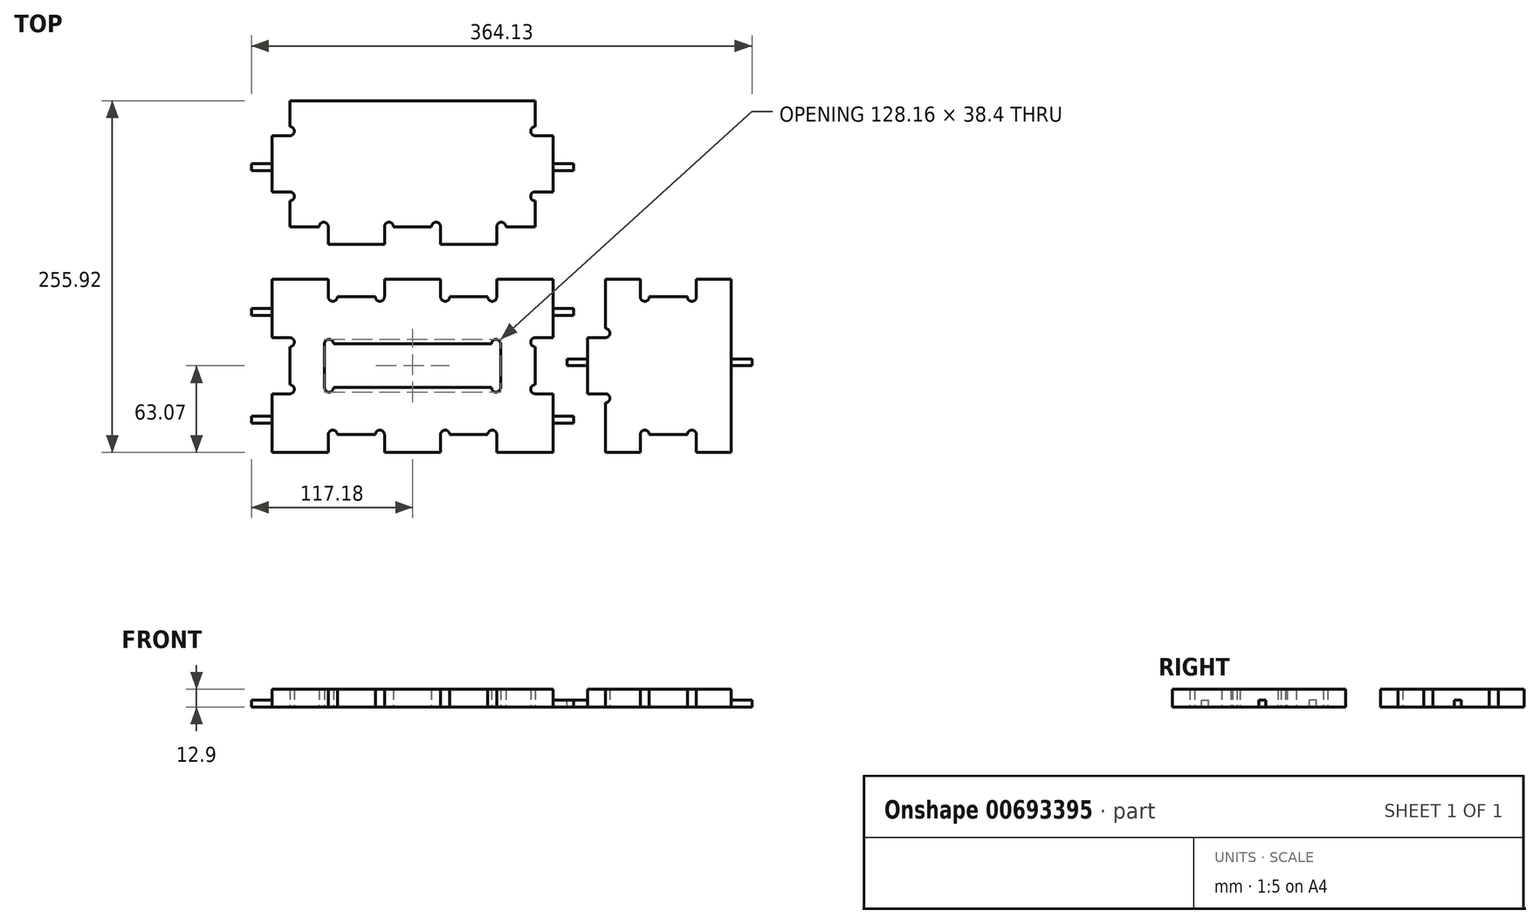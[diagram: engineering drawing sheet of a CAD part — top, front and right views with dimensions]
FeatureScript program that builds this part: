
annotation { "Feature Type Name" : "Feature", "Feature Type Description" : "" }
export const myFeature = defineFeature(function(context is Context, id is Id, definition is map)
    precondition{}
    {
        {
            assignVariable(context, id + "F0", {"name" : "thick", "anyValue" : 12.9 * mm});
        }
        {
            var Q0;
            Q0=qCreatedBy(makeId("Top.planeOp"),FACE);
            var sketch = newSketch(context, id + "F1", { "sketchPlane" : qUnion([Q0])});
            skLineSegment(sketch, "E0.bottom", {"start": v(64.08, -15.9) * mm, "end": v(-64.08, -15.9) * mm});
            skLineSegment(sketch, "E0.top", {"start": v(64.08, 15.9) * mm, "end": v(-64.08, 15.9) * mm});
            skLineSegment(sketch, "E0.left", {"start": v(64.08, -15.9) * mm, "end": v(64.08, 15.9) * mm});
            skLineSegment(sketch, "E0.right", {"start": v(-64.08, -15.9) * mm, "end": v(-64.08, 15.9) * mm});
            skPoint(sketch, "E0.middle", {"position": v(0, 0) * mm});
            skLineSegment(sketch, "E1", {"start": v(-102.18, 63.07) * mm, "end": v(-61.3, 63.07) * mm});
            skLineSegment(sketch, "E2", {"start": v(102.18, 63.07) * mm, "end": v(102.18, -63.07) * mm});
            skLineSegment(sketch, "E3", {"start": v(102.18, -63.07) * mm, "end": v(-102.18, -63.07) * mm});
            skLineSegment(sketch, "E4", {"start": v(-102.18, -63.07) * mm, "end": v(-102.18, 63.07) * mm});
            skPoint(sketch, "E5", {"position": v(0, 63.07) * mm});
            skPoint(sketch, "E6", {"position": v(102.18, 0) * mm});
            skLineSegment(sketch, "E7", {"start": v(-102.18, -63.07) * mm, "end": v(102.18, 63.07) * mm, "construction": true});
            skCircle(sketch, "E8", {"center": v(-60.78, 15.9) * mm, "radius": 3.3 * mm});
            skCircle(sketch, "E9", {"center": v(-60.78, -15.9) * mm, "radius": 3.3 * mm});
            skCircle(sketch, "E10", {"center": v(60.78, -15.9) * mm, "radius": 3.3 * mm});
            skCircle(sketch, "E11", {"center": v(60.78, 15.9) * mm, "radius": 3.3 * mm});
            skLineSegment(sketch, "E12", {"start": v(-61.3, 50.17) * mm, "end": v(-20.44, 50.17) * mm});
            skLineSegment(sketch, "E13", {"start": v(20.44, 50.17) * mm, "end": v(61.3, 50.17) * mm});
            skLineSegment(sketch, "E14", {"start": v(-61.3, 50.17) * mm, "end": v(-61.3, 63.07) * mm});
            skLineSegment(sketch, "E15", {"start": v(-20.44, 50.17) * mm, "end": v(-20.44, 63.07) * mm});
            skLineSegment(sketch, "E16", {"start": v(20.44, 50.17) * mm, "end": v(20.44, 63.07) * mm});
            skLineSegment(sketch, "E17", {"start": v(61.3, 50.17) * mm, "end": v(61.3, 63.07) * mm});
            skLineSegment(sketch, "E18", {"start": v(-61.3, 63.07) * mm, "end": v(-20.44, 63.07) * mm});
            skLineSegment(sketch, "E19", {"start": v(-20.44, 63.07) * mm, "end": v(20.44, 63.07) * mm});
            skLineSegment(sketch, "E20", {"start": v(20.44, 63.07) * mm, "end": v(61.3, 63.07) * mm});
            skLineSegment(sketch, "E21", {"start": v(61.3, 63.07) * mm, "end": v(102.18, 63.07) * mm});
            skLineSegment(sketch, "E22", {"start": v(-61.3, -63.07) * mm, "end": v(-61.3, -50.17) * mm});
            skLineSegment(sketch, "E23", {"start": v(-61.3, -50.17) * mm, "end": v(-20.44, -50.17) * mm});
            skLineSegment(sketch, "E24", {"start": v(-20.44, -50.17) * mm, "end": v(-20.44, -63.07) * mm});
            skLineSegment(sketch, "E25", {"start": v(20.44, -63.07) * mm, "end": v(20.44, -50.17) * mm});
            skLineSegment(sketch, "E26", {"start": v(20.44, -50.17) * mm, "end": v(61.3, -50.17) * mm});
            skLineSegment(sketch, "E27", {"start": v(61.3, -50.17) * mm, "end": v(61.3, -63.07) * mm});
            skLineSegment(sketch, "E28", {"start": v(102.18, 20.44) * mm, "end": v(89.28, 20.44) * mm});
            skLineSegment(sketch, "E29", {"start": v(89.28, 20.44) * mm, "end": v(89.28, -20.44) * mm});
            skLineSegment(sketch, "E30", {"start": v(89.28, -20.44) * mm, "end": v(102.18, -20.44) * mm});
            skPoint(sketch, "E31", {"position": v(89.28, 0) * mm});
            skLineSegment(sketch, "E32", {"start": v(-102.18, 20.44) * mm, "end": v(-89.28, 20.44) * mm});
            skLineSegment(sketch, "E33", {"start": v(-89.28, 20.44) * mm, "end": v(-89.28, -20.44) * mm});
            skLineSegment(sketch, "E34", {"start": v(-89.28, -20.44) * mm, "end": v(-102.18, -20.44) * mm});
            skCircle(sketch, "E35", {"center": v(-58, 50.17) * mm, "radius": 3.3 * mm});
            skCircle(sketch, "E36", {"center": v(-23.74, 50.17) * mm, "radius": 3.3 * mm});
            skCircle(sketch, "E37", {"center": v(23.74, 50.17) * mm, "radius": 3.3 * mm});
            skCircle(sketch, "E38", {"center": v(58, 50.17) * mm, "radius": 3.3 * mm});
            skCircle(sketch, "E39", {"center": v(89.28, 17.13) * mm, "radius": 3.3 * mm});
            skCircle(sketch, "E40", {"center": v(89.28, -17.13) * mm, "radius": 3.3 * mm});
            skCircle(sketch, "E41", {"center": v(58, -50.17) * mm, "radius": 3.3 * mm});
            skCircle(sketch, "E42", {"center": v(23.74, -50.17) * mm, "radius": 3.3 * mm});
            skCircle(sketch, "E43", {"center": v(-23.74, -50.17) * mm, "radius": 3.3 * mm});
            skCircle(sketch, "E44", {"center": v(-58, -50.17) * mm, "radius": 3.3 * mm});
            skCircle(sketch, "E45", {"center": v(-89.28, -17.13) * mm, "radius": 3.3 * mm});
            skCircle(sketch, "E46", {"center": v(-89.28, 17.13) * mm, "radius": 3.3 * mm});
            skLineSegment(sketch, "E47", {"start": v(-89.28, 101.17) * mm, "end": v(89.28, 101.17) * mm});
            skLineSegment(sketch, "E48", {"start": v(89.28, 101.17) * mm, "end": v(89.28, 192.85) * mm});
            skLineSegment(sketch, "E49", {"start": v(89.28, 192.85) * mm, "end": v(-89.28, 192.85) * mm});
            skLineSegment(sketch, "E50", {"start": v(-89.28, 192.85) * mm, "end": v(-89.28, 101.17) * mm});
            skLineSegment(sketch, "E51", {"start": v(-61.3, 101.17) * mm, "end": v(-61.3, 88.27) * mm});
            skLineSegment(sketch, "E52", {"start": v(-61.3, 88.27) * mm, "end": v(-20.44, 88.27) * mm});
            skLineSegment(sketch, "E53", {"start": v(-20.44, 88.27) * mm, "end": v(-20.44, 101.17) * mm});
            skLineSegment(sketch, "E54", {"start": v(20.44, 101.17) * mm, "end": v(20.44, 88.27) * mm});
            skLineSegment(sketch, "E55", {"start": v(20.44, 88.27) * mm, "end": v(61.3, 88.27) * mm});
            skLineSegment(sketch, "E56", {"start": v(61.3, 88.27) * mm, "end": v(61.3, 101.17) * mm});
            skCircle(sketch, "E57", {"center": v(17.13, 101.17) * mm, "radius": 3.3 * mm});
            skCircle(sketch, "E58", {"center": v(-17.13, 101.17) * mm, "radius": 3.3 * mm});
            skCircle(sketch, "E59", {"center": v(-64.61, 101.17) * mm, "radius": 3.3 * mm});
            skCircle(sketch, "E60", {"center": v(64.61, 101.17) * mm, "radius": 3.3 * mm});
            skLineSegment(sketch, "E61", {"start": v(102.18, 167.45) * mm, "end": v(102.18, 126.57) * mm});
            skPoint(sketch, "E62", {"position": v(89.28, 147.01) * mm});
            skPoint(sketch, "E63", {"position": v(102.18, 147.01) * mm});
            skLineSegment(sketch, "E64", {"start": v(102.18, 167.45) * mm, "end": v(89.28, 167.45) * mm});
            skLineSegment(sketch, "E65", {"start": v(102.18, 126.57) * mm, "end": v(89.28, 126.57) * mm});
            skCircle(sketch, "E66", {"center": v(89.28, 123.27) * mm, "radius": 3.3 * mm});
            skCircle(sketch, "E67", {"center": v(89.28, 170.75) * mm, "radius": 3.3 * mm});
            skLineSegment(sketch, "E68", {"start": v(-89.28, 126.57) * mm, "end": v(-102.18, 126.57) * mm});
            skLineSegment(sketch, "E69", {"start": v(-102.18, 126.57) * mm, "end": v(-102.18, 167.45) * mm});
            skLineSegment(sketch, "E70", {"start": v(-102.18, 167.45) * mm, "end": v(-89.28, 167.45) * mm});
            skCircle(sketch, "E71", {"center": v(-89.28, 170.75) * mm, "radius": 3.3 * mm});
            skCircle(sketch, "E72", {"center": v(-89.28, 123.27) * mm, "radius": 3.3 * mm});
            skLineSegment(sketch, "E73", {"start": v(140.28, 63.07) * mm, "end": v(140.28, -63.07) * mm});
            skLineSegment(sketch, "E74", {"start": v(231.95, -63.07) * mm, "end": v(231.95, 63.07) * mm});
            skLineSegment(sketch, "E75", {"start": v(231.95, 63.07) * mm, "end": v(140.28, 63.07) * mm});
            skLineSegment(sketch, "E76", {"start": v(140.28, 20.44) * mm, "end": v(127.38, 20.44) * mm});
            skLineSegment(sketch, "E77", {"start": v(127.38, 20.44) * mm, "end": v(127.38, -20.44) * mm});
            skLineSegment(sketch, "E78", {"start": v(127.38, -20.44) * mm, "end": v(140.28, -20.44) * mm});
            skLineSegment(sketch, "E79", {"start": v(140.28, -63.07) * mm, "end": v(231.95, -63.07) * mm});
            skLineSegment(sketch, "E80", {"start": v(165.68, 63.07) * mm, "end": v(165.68, 50.17) * mm});
            skLineSegment(sketch, "E81", {"start": v(165.68, 50.17) * mm, "end": v(206.55, 50.17) * mm});
            skLineSegment(sketch, "E82", {"start": v(206.55, 50.17) * mm, "end": v(206.55, 63.07) * mm});
            skLineSegment(sketch, "E83", {"start": v(165.68, -63.07) * mm, "end": v(165.68, -50.17) * mm});
            skLineSegment(sketch, "E84", {"start": v(165.68, -50.17) * mm, "end": v(206.55, -50.17) * mm});
            skLineSegment(sketch, "E85", {"start": v(206.55, -50.17) * mm, "end": v(206.55, -63.07) * mm});
            skPoint(sketch, "E86", {"position": v(186.12, 50.17) * mm});
            skPoint(sketch, "E87", {"position": v(186.12, 63.07) * mm});
            skCircle(sketch, "E88", {"center": v(140.28, 23.74) * mm, "radius": 3.3 * mm});
            skCircle(sketch, "E89", {"center": v(140.28, -23.74) * mm, "radius": 3.3 * mm});
            skCircle(sketch, "E90", {"center": v(168.98, -50.17) * mm, "radius": 3.3 * mm});
            skCircle(sketch, "E91", {"center": v(203.25, -50.17) * mm, "radius": 3.3 * mm});
            skCircle(sketch, "E92", {"center": v(203.25, 50.17) * mm, "radius": 3.3 * mm});
            skCircle(sketch, "E93", {"center": v(168.98, 50.17) * mm, "radius": 3.3 * mm});
            skLineSegment(sketch, "E94", {"start": v(-89.28, 101.17) * mm, "end": v(-89.28, 63.07) * mm, "construction": true});
            skLineSegment(sketch, "E95", {"start": v(89.28, 101.17) * mm, "end": v(89.28, 63.07) * mm, "construction": true});
            skLineSegment(sketch, "E96", {"start": v(-89.28, 82.12) * mm, "end": v(89.28, 82.12) * mm, "construction": true});
            skSolve(sketch);
        }
        {
            var Q0;
            {var subQ48=sQuery(id+"F1.wireOp",EDGE,"E0.left");Q0=makeQuery(id+"F1.imprint","IMPRINT",FACE,{"disambiguationData":[TD([[makeQuery(id+"F1.imprint","IMPRINT",EDGE,{"derivedFrom":subQ48}),-1.0]])]});}
            extrude(context, id + "F2", {"entities" : qUnion([Q0]), "depth" : getVariable(context, 'thick'), "offsetDistance" : 25 * mm});
        }
        {
            var Q0;
            {var subQ0=sQuery(id+"F1.wireOp",EDGE,"E49");Q0=makeQuery(id+"F1.imprint","IMPRINT",FACE,{"disambiguationData":[TD([[makeQuery(id+"F1.imprint","IMPRINT",EDGE,{"derivedFrom":subQ0}),1.0]])]});}
            var Q1;
            {var subQ0=sQuery(id+"F1.wireOp",EDGE,"E68");Q1=makeQuery(id+"F1.imprint","IMPRINT",FACE,{"disambiguationData":[TD([[makeQuery(id+"F1.imprint","IMPRINT",EDGE,{"derivedFrom":subQ0}),-1.0]])]});}
            var Q2;
            {var subQ0=sQuery(id+"F1.wireOp",EDGE,"E51");Q2=makeQuery(id+"F1.imprint","IMPRINT",FACE,{"disambiguationData":[TD([[makeQuery(id+"F1.imprint","IMPRINT",EDGE,{"derivedFrom":subQ0}),1.0]])]});}
            var Q3;
            {var subQ0=sQuery(id+"F1.wireOp",EDGE,"E54");Q3=makeQuery(id+"F1.imprint","IMPRINT",FACE,{"disambiguationData":[TD([[makeQuery(id+"F1.imprint","IMPRINT",EDGE,{"derivedFrom":subQ0}),1.0]])]});}
            var Q4;
            Q4=makeQuery(id+"F1.imprint","IMPRINT",FACE,{"disambiguationData":[TD([[makeQuery(id+"F1.imprint","IMPRINT",EDGE,{"derivedFrom":sQuery(id+"F1.wireOp",EDGE,"E61")}),-1.0]])]});
            extrude(context, id + "F3", {"entities" : qUnion([Q0, Q1, Q2, Q3, Q4]), "depth" : getVariable(context, 'thick'), "offsetDistance" : 25 * mm});
        }
        {
            var Q0;
            {var subQ1=sQuery(id+"F1.wireOp",EDGE,"E74");Q0=makeQuery(id+"F1.imprint","IMPRINT",FACE,{"disambiguationData":[TD([[makeQuery(id+"F1.imprint","IMPRINT",EDGE,{"derivedFrom":subQ1}),1.0]])]});}
            var Q1;
            {var subQ0=sQuery(id+"F1.wireOp",EDGE,"E76");Q1=makeQuery(id+"F1.imprint","IMPRINT",FACE,{"disambiguationData":[TD([[makeQuery(id+"F1.imprint","IMPRINT",EDGE,{"derivedFrom":subQ0}),1.0]])]});}
            extrude(context, id + "F4", {"entities" : qUnion([Q0, Q1]), "depth" : getVariable(context, 'thick'), "offsetDistance" : 25 * mm});
        }
        {
            var Q0;
            {var subQ0=sQuery(id+"F1.wireOp",EDGE,"E4");Q0=makeQuery(id+"F2.opExtrude","SWEPT_FACE",FACE,{"disambiguationData":[OSD([subQ0]),TDD([makeQuery(id+"F1.imprint","IMPRINT",EDGE,{"disambiguationData":[TD([[makeQuery(id+"F1.imprint","INTERSECT",VERTEX,{"derivedFrom":[sQuery(id+"F1.wireOp",EDGE,"E1"),subQ0]}),1.0]])],"derivedFrom":subQ0})])]});}
            var sketch = newSketch(context, id + "F5", { "sketchPlane" : qUnion([Q0])});
            skLineSegment(sketch, "E97", {"start": v(-41.76, 5) * mm, "end": v(-36.76, 5) * mm});
            skLineSegment(sketch, "E98", {"start": v(-36.76, 5) * mm, "end": v(-36.76, 0) * mm});
            skLineSegment(sketch, "E99", {"start": v(-36.76, 0) * mm, "end": v(-41.76, 0) * mm});
            skLineSegment(sketch, "E100", {"start": v(-41.76, 0) * mm, "end": v(-41.76, 5) * mm});
            skSolve(sketch);
        }
        {
            var Q0;
            Q0=makeQuery(id+"F5.imprint","IMPRINT",FACE,{"disambiguationData":[TD([[makeQuery(id+"F5.imprint","IMPRINT",EDGE,{"derivedFrom":sQuery(id+"F5.wireOp",EDGE,"E97")}),-1.0]])]});
            extrude(context, id + "F6", {"entities" : qUnion([Q0]), "operationType" : NewBodyOperationType.ADD, "depth" : 15 * mm, "offsetDistance" : 25 * mm});
        }
        {
            var Q0;
            {var subQ0=sQuery(id+"F1.wireOp",EDGE,"E4");Q0=makeQuery(id+"F2.opExtrude","SWEPT_FACE",FACE,{"disambiguationData":[OSD([subQ0]),TDD([makeQuery(id+"F1.imprint","IMPRINT",EDGE,{"disambiguationData":[TD([[makeQuery(id+"F1.imprint","INTERSECT",VERTEX,{"derivedFrom":[sQuery(id+"F1.wireOp",EDGE,"E3"),subQ0]}),-1.0]])],"derivedFrom":subQ0})])]});}
            var sketch = newSketch(context, id + "F7", { "sketchPlane" : qUnion([Q0])});
            skLineSegment(sketch, "E101.bottom", {"start": v(41.76, 0) * mm, "end": v(36.76, 0) * mm});
            skLineSegment(sketch, "E101.top", {"start": v(41.76, 5) * mm, "end": v(36.76, 5) * mm});
            skLineSegment(sketch, "E101.left", {"start": v(41.76, 0) * mm, "end": v(41.76, 5) * mm});
            skLineSegment(sketch, "E101.right", {"start": v(36.76, 0) * mm, "end": v(36.76, 5) * mm});
            skSolve(sketch);
        }
        {
            var Q0;
            Q0=makeQuery(id+"F7.imprint","IMPRINT",FACE,{"disambiguationData":[TD([[makeQuery(id+"F7.imprint","IMPRINT",EDGE,{"derivedFrom":sQuery(id+"F7.wireOp",EDGE,"E101.bottom")}),-1.0]])]});
            extrude(context, id + "F8", {"entities" : qUnion([Q0]), "operationType" : NewBodyOperationType.ADD, "depth" : 15 * mm, "offsetDistance" : 25 * mm});
        }
        {
            var Q0;
            {var subQ0=sQuery(id+"F1.wireOp",EDGE,"E2");Q0=makeQuery(id+"F2.opExtrude","SWEPT_FACE",FACE,{"disambiguationData":[OSD([subQ0]),TDD([makeQuery(id+"F1.imprint","IMPRINT",EDGE,{"disambiguationData":[TD([[makeQuery(id+"F1.imprint","INTERSECT",VERTEX,{"derivedFrom":[subQ0,sQuery(id+"F1.wireOp",EDGE,"E3")]}),1.0]])],"derivedFrom":subQ0})])]});}
            var sketch = newSketch(context, id + "F9", { "sketchPlane" : qUnion([Q0])});
            skLineSegment(sketch, "E102.bottom", {"start": v(-41.76, 0) * mm, "end": v(-36.76, 0) * mm});
            skLineSegment(sketch, "E102.top", {"start": v(-41.76, 5) * mm, "end": v(-36.76, 5) * mm});
            skLineSegment(sketch, "E102.left", {"start": v(-41.76, 0) * mm, "end": v(-41.76, 5) * mm});
            skLineSegment(sketch, "E102.right", {"start": v(-36.76, 0) * mm, "end": v(-36.76, 5) * mm});
            skSolve(sketch);
        }
        {
            var Q0;
            Q0=makeQuery(id+"F9.imprint","IMPRINT",FACE,{"disambiguationData":[TD([[makeQuery(id+"F9.imprint","IMPRINT",EDGE,{"derivedFrom":sQuery(id+"F9.wireOp",EDGE,"E102.bottom")}),-1.0]])]});
            extrude(context, id + "F10", {"entities" : qUnion([Q0]), "operationType" : NewBodyOperationType.ADD, "depth" : 15 * mm, "offsetDistance" : 25 * mm});
        }
        {
            var Q0;
            {var subQ0=sQuery(id+"F1.wireOp",EDGE,"E2");Q0=makeQuery(id+"F2.opExtrude","SWEPT_FACE",FACE,{"disambiguationData":[OSD([subQ0]),TDD([makeQuery(id+"F1.imprint","IMPRINT",EDGE,{"disambiguationData":[TD([[makeQuery(id+"F1.imprint","INTERSECT",VERTEX,{"derivedFrom":[subQ0,sQuery(id+"F1.wireOp",EDGE,"E21")]}),-1.0]])],"derivedFrom":subQ0})])]});}
            var sketch = newSketch(context, id + "F11", { "sketchPlane" : qUnion([Q0])});
            skLineSegment(sketch, "E103.bottom", {"start": v(41.76, 0) * mm, "end": v(36.76, 0) * mm});
            skLineSegment(sketch, "E103.top", {"start": v(41.76, 5) * mm, "end": v(36.76, 5) * mm});
            skLineSegment(sketch, "E103.left", {"start": v(41.76, 0) * mm, "end": v(41.76, 5) * mm});
            skLineSegment(sketch, "E103.right", {"start": v(36.76, 0) * mm, "end": v(36.76, 5) * mm});
            skSolve(sketch);
        }
        {
            var Q0;
            Q0 = qSketchRegion(id + "F11", true);
            extrude(context, id + "F12", {"entities" : qUnion([Q0]), "operationType" : NewBodyOperationType.ADD, "depth" : 15 * mm, "offsetDistance" : 25 * mm});
        }
        {
            var Q0;
            Q0=makeQuery(id+"F3.opExtrude","SWEPT_FACE",FACE,{"disambiguationData":[OSD([sQuery(id+"F1.wireOp",EDGE,"E69")])]});
            var sketch = newSketch(context, id + "F13", { "sketchPlane" : qUnion([Q0])});
            skLineSegment(sketch, "E104.bottom", {"start": v(-147.01, 0) * mm, "end": v(-142.01, 0) * mm});
            skLineSegment(sketch, "E104.top", {"start": v(-147.01, 5) * mm, "end": v(-142.01, 5) * mm});
            skLineSegment(sketch, "E104.left", {"start": v(-147.01, 0) * mm, "end": v(-147.01, 5) * mm});
            skLineSegment(sketch, "E104.right", {"start": v(-142.01, 0) * mm, "end": v(-142.01, 5) * mm});
            skSolve(sketch);
        }
        {
            var Q0;
            Q0 = qSketchRegion(id + "F13", true);
            var Q1;
            Q1=makeQuery(id+"F13.imprint","IMPRINT",FACE,{"disambiguationData":[TD([[makeQuery(id+"F13.imprint","IMPRINT",EDGE,{"derivedFrom":sQuery(id+"F13.wireOp",EDGE,"E104.bottom")}),-1.0]])]});
            extrude(context, id + "F14", {"entities" : qUnion([Q0, Q1]), "operationType" : NewBodyOperationType.ADD, "depth" : 15 * mm, "offsetDistance" : 25 * mm});
        }
        {
            var Q0;
            Q0=makeQuery(id+"F3.opExtrude","SWEPT_FACE",FACE,{"disambiguationData":[OSD([sQuery(id+"F1.wireOp",EDGE,"E61")])]});
            var sketch = newSketch(context, id + "F15", { "sketchPlane" : qUnion([Q0])});
            skLineSegment(sketch, "E105.bottom", {"start": v(147.01, 0) * mm, "end": v(142.01, 0) * mm});
            skLineSegment(sketch, "E105.top", {"start": v(147.01, 5) * mm, "end": v(142.01, 5) * mm});
            skLineSegment(sketch, "E105.left", {"start": v(147.01, 0) * mm, "end": v(147.01, 5) * mm});
            skLineSegment(sketch, "E105.right", {"start": v(142.01, 0) * mm, "end": v(142.01, 5) * mm});
            skSolve(sketch);
        }
        {
            var Q0;
            Q0 = qSketchRegion(id + "F15", true);
            extrude(context, id + "F16", {"entities" : qUnion([Q0]), "operationType" : NewBodyOperationType.ADD, "depth" : 15 * mm, "offsetDistance" : 25 * mm});
        }
        {
            var Q0;
            Q0=makeQuery(id+"F4.opExtrude","SWEPT_FACE",FACE,{"disambiguationData":[OSD([sQuery(id+"F1.wireOp",EDGE,"E77")])]});
            var sketch = newSketch(context, id + "F17", { "sketchPlane" : qUnion([Q0])});
            skLineSegment(sketch, "E106.bottom", {"start": v(0, 0) * mm, "end": v(-5, 0) * mm});
            skLineSegment(sketch, "E106.top", {"start": v(0, 5) * mm, "end": v(-5, 5) * mm});
            skLineSegment(sketch, "E106.left", {"start": v(0, 0) * mm, "end": v(0, 5) * mm});
            skLineSegment(sketch, "E106.right", {"start": v(-5, 0) * mm, "end": v(-5, 5) * mm});
            skSolve(sketch);
        }
        {
            var Q0;
            Q0=makeQuery(id+"F17.imprint","IMPRINT",FACE,{"disambiguationData":[TD([[makeQuery(id+"F17.imprint","IMPRINT",EDGE,{"derivedFrom":sQuery(id+"F17.wireOp",EDGE,"E106.bottom")}),1.0]])]});
            extrude(context, id + "F18", {"entities" : qUnion([Q0]), "operationType" : NewBodyOperationType.ADD, "depth" : 15 * mm, "offsetDistance" : 25 * mm});
        }
        {
            var Q0;
            Q0=makeQuery(id+"F4.opExtrude","SWEPT_FACE",FACE,{"disambiguationData":[OSD([sQuery(id+"F1.wireOp",EDGE,"E74")])]});
            var sketch = newSketch(context, id + "F19", { "sketchPlane" : qUnion([Q0])});
            skLineSegment(sketch, "E107.bottom", {"start": v(0, 0) * mm, "end": v(5, 0) * mm});
            skLineSegment(sketch, "E107.top", {"start": v(0, 5) * mm, "end": v(5, 5) * mm});
            skLineSegment(sketch, "E107.left", {"start": v(0, 0) * mm, "end": v(0, 5) * mm});
            skLineSegment(sketch, "E107.right", {"start": v(5, 0) * mm, "end": v(5, 5) * mm});
            skSolve(sketch);
        }
        {
            var Q0;
            Q0=makeQuery(id+"F19.imprint","IMPRINT",FACE,{"disambiguationData":[TD([[makeQuery(id+"F19.imprint","IMPRINT",EDGE,{"derivedFrom":sQuery(id+"F19.wireOp",EDGE,"E107.bottom")}),1.0]])]});
            extrude(context, id + "F20", {"entities" : qUnion([Q0]), "operationType" : NewBodyOperationType.ADD, "depth" : 15 * mm, "offsetDistance" : 25 * mm});
        }
    });
